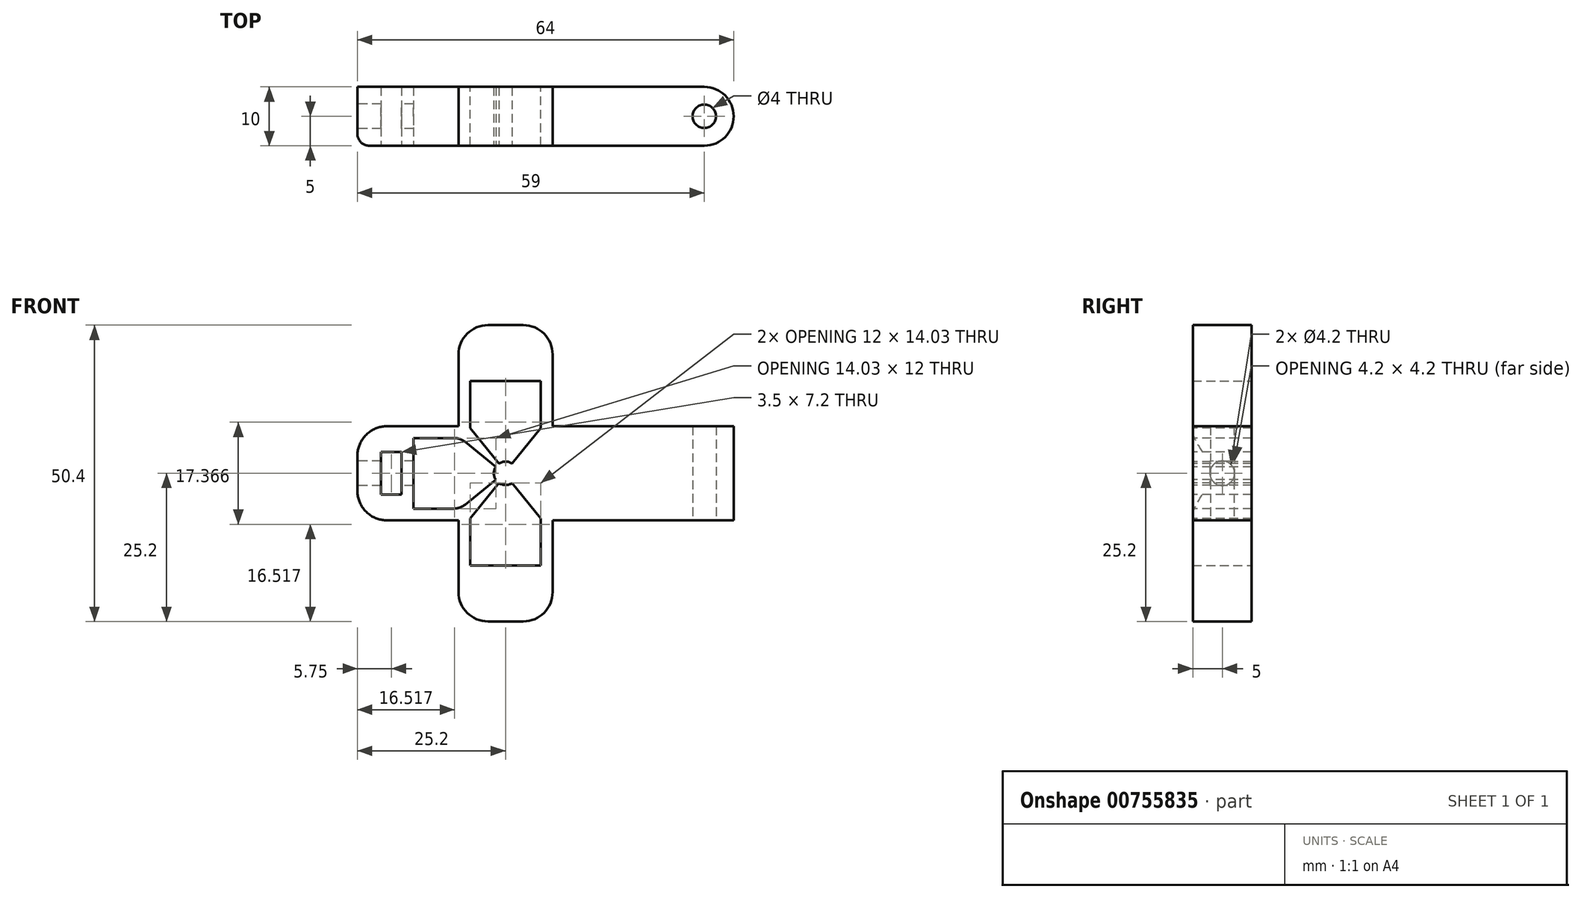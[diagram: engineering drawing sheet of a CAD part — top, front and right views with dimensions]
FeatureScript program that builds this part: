
annotation { "Feature Type Name" : "Feature", "Feature Type Description" : "" }
export const myFeature = defineFeature(function(context is Context, id is Id, definition is map)
    precondition{}
    {
        {
            var Q0;
            Q0=qCreatedBy(makeId("Top.planeOp"),FACE);
            var sketch = newSketch(context, id + "F0", { "sketchPlane" : qUnion([Q0])});
            skLineSegment(sketch, "E0.bottom", {"start": v(32, 5) * mm, "end": v(-32, 5) * mm});
            skLineSegment(sketch, "E0.top", {"start": v(32, -5) * mm, "end": v(-30, -5) * mm});
            skLineSegment(sketch, "E0.left", {"start": v(32, 5) * mm, "end": v(32, -5) * mm});
            skLineSegment(sketch, "E0.right", {"start": v(-32, 5) * mm, "end": v(-32, -3) * mm});
            skPoint(sketch, "E0.middle", {"position": v(0, 0) * mm});
            skCircle(sketch, "E1", {"center": v(27, 0) * mm, "radius": 2 * mm});
            skLineSegment(sketch, "E2", {"start": v(18, 5) * mm, "end": v(18, 19.7) * mm});
            skLineSegment(sketch, "E3", {"start": v(18, 19.7) * mm, "end": v(8, 19.7) * mm});
            skLineSegment(sketch, "E4", {"start": v(8, 19.7) * mm, "end": v(8, 5) * mm});
            skArc(sketch, "E5", {"start": v(27, -5) * mm, "mid": v(32, 0) * mm, "end": v(27, 5) * mm});
            skArc(sketch, "E6", {"start": v(-32, -3) * mm, "mid": v(-31.41, -4.41) * mm, "end": v(-30, -5) * mm});
            skLineSegment(sketch, "E7", {"start": v(-30, -3) * mm, "end": v(-30, -5) * mm});
            skLineSegment(sketch, "E8", {"start": v(-30, -3) * mm, "end": v(-32, -3) * mm});
            skSolve(sketch);
        }
        {
            var Q0;
            Q0=makeQuery(id+"F0.imprint","IMPRINT",FACE,{"disambiguationData":[TD([[makeQuery(id+"F0.imprint","IMPRINT",EDGE,{"derivedFrom":sQuery(id+"F0.wireOp",EDGE,"E0.bottom")}),1.0]])]});
            var Q1;
            Q1=makeQuery(id+"F0.imprint","IMPRINT",FACE,{"disambiguationData":[TD([[makeQuery(id+"F0.imprint","IMPRINT",EDGE,{"derivedFrom":sQuery(id+"F0.wireOp",EDGE,"E6")}),1.0]])]});
            extrude(context, id + "F1", {"entities" : qUnion([Q0, Q1]), "depth" : 16 * mm, "offsetDistance" : 25 * mm});
        }
        {
            var Q0;
            Q0=qCreatedBy(makeId("Front.planeOp"),FACE);
            var sketch = newSketch(context, id + "F2", { "sketchPlane" : qUnion([Q0])});
            skLineSegment(sketch, "E9.bottom", {"start": v(-27, 0) * mm, "end": v(32, 0) * mm});
            skLineSegment(sketch, "E9.top", {"start": v(-27, 16) * mm, "end": v(32, 16) * mm});
            skLineSegment(sketch, "E9.left", {"start": v(-32, 5) * mm, "end": v(-32, 11) * mm});
            skLineSegment(sketch, "E9.right", {"start": v(32, 0) * mm, "end": v(32, 16) * mm});
            skArc(sketch, "E10", {"start": v(-27, 16) * mm, "mid": v(-30.54, 14.54) * mm, "end": v(-32, 11) * mm});
            skArc(sketch, "E11", {"start": v(-32, 5) * mm, "mid": v(-30.54, 1.46) * mm, "end": v(-27, 0) * mm});
            skLineSegment(sketch, "E12.bottom", {"start": v(-28, 11.6) * mm, "end": v(-24.5, 11.6) * mm});
            skLineSegment(sketch, "E12.top", {"start": v(-28, 4.4) * mm, "end": v(-24.5, 4.4) * mm});
            skLineSegment(sketch, "E12.left", {"start": v(-28, 11.6) * mm, "end": v(-28, 4.4) * mm});
            skLineSegment(sketch, "E12.right", {"start": v(-24.5, 11.6) * mm, "end": v(-24.5, 4.4) * mm});
            skPoint(sketch, "E12.middle", {"position": v(-26.25, 8) * mm});
            skLineSegment(sketch, "E13.bottom", {"start": v(-22.5, 2) * mm, "end": v(-7.1, 2) * mm});
            skLineSegment(sketch, "E13.top", {"start": v(-22.5, 14) * mm, "end": v(-7.1, 14) * mm});
            skLineSegment(sketch, "E13.left", {"start": v(-22.5, 2) * mm, "end": v(-22.5, 14) * mm});
            skLineSegment(sketch, "E13.right", {"start": v(-7.1, 2) * mm, "end": v(-7.1, 14) * mm});
            skPoint(sketch, "E13.middle", {"position": v(-14.8, 8) * mm});
            skLineSegment(sketch, "E14", {"start": v(-7.1, 8) * mm, "end": v(-14.5, 14) * mm});
            skPoint(sketch, "E15.MirrorP", {"position": v(-8.7, 15.53) * mm});
            skLineSegment(sketch, "E16", {"start": v(-7.1, 8) * mm, "end": v(-14.5, 2) * mm});
            skPoint(sketch, "E16.endSnap0", {"position": v(-14.8, 2) * mm});
            skLineSegment(sketch, "E17", {"start": v(-27, 16) * mm, "end": v(-32, 16) * mm});
            skLineSegment(sketch, "E18", {"start": v(-32, 16) * mm, "end": v(-32, 11) * mm});
            skLineSegment(sketch, "E19", {"start": v(-32, 5) * mm, "end": v(-32, 0) * mm});
            skLineSegment(sketch, "E20", {"start": v(-32, 0) * mm, "end": v(-32, 5) * mm});
            skLineSegment(sketch, "E21", {"start": v(-32, 0) * mm, "end": v(-27, 0) * mm});
            skLineSegment(sketch, "E22.1.0", {"start": v(-6.8, 8.3) * mm, "end": v(-0.8, 15.7) * mm});
            skLineSegment(sketch, "E22.1.1", {"start": v(-0.8, 23.7) * mm, "end": v(-0.8, 8.3) * mm});
            skLineSegment(sketch, "E22.1.2", {"start": v(-12.8, 23.7) * mm, "end": v(-0.8, 23.7) * mm});
            skLineSegment(sketch, "E22.1.3", {"start": v(-12.8, 23.7) * mm, "end": v(-12.8, 8.3) * mm});
            skLineSegment(sketch, "E22.1.4", {"start": v(-6.8, 8.3) * mm, "end": v(-12.8, 15.7) * mm});
            skPoint(sketch, "E22.center", {"position": v(-6.8, 8) * mm});
            skLineSegment(sketch, "E22.anchor1", {"start": v(-6.8, 8) * mm, "end": v(-22.5, 2) * mm, "construction": true});
            skLineSegment(sketch, "E22.anchor2", {"start": v(-6.8, 8) * mm, "end": v(-12.8, 23.7) * mm, "construction": true});
            skLineSegment(sketch, "E23.1.0", {"start": v(-12.8, -7.7) * mm, "end": v(-12.8, 7.7) * mm});
            skLineSegment(sketch, "E23.1.1", {"start": v(-6.8, 7.7) * mm, "end": v(-12.8, 0.3) * mm});
            skLineSegment(sketch, "E23.1.2", {"start": v(-6.8, 7.7) * mm, "end": v(-0.8, 0.3) * mm});
            skLineSegment(sketch, "E23.1.3", {"start": v(-0.8, -7.7) * mm, "end": v(-0.8, 7.7) * mm});
            skLineSegment(sketch, "E23.1.4", {"start": v(-0.8, -7.7) * mm, "end": v(-12.8, -7.7) * mm});
            skLineSegment(sketch, "E24", {"start": v(1.2, 16) * mm, "end": v(1.2, 33.2) * mm});
            skLineSegment(sketch, "E25", {"start": v(1.2, 33.2) * mm, "end": v(-14.8, 33.2) * mm});
            skLineSegment(sketch, "E26", {"start": v(-14.8, 33.2) * mm, "end": v(-14.8, 16) * mm});
            skLineSegment(sketch, "E27", {"start": v(1.2, 0) * mm, "end": v(1.2, -17.2) * mm});
            skLineSegment(sketch, "E28", {"start": v(1.2, -17.2) * mm, "end": v(-14.8, -17.2) * mm});
            skLineSegment(sketch, "E29", {"start": v(-14.8, -17.2) * mm, "end": v(-14.8, 0) * mm});
            skCircle(sketch, "E30", {"center": v(-6.8, 8) * mm, "radius": 2 * mm});
            skSolve(sketch);
        }
        {
            var Q0;
            Q0=makeQuery(id+"F2.imprint","IMPRINT",FACE,{"disambiguationData":[TD([[makeQuery(id+"F2.imprint","IMPRINT",EDGE,{"derivedFrom":sQuery(id+"F2.wireOp",EDGE,"E10")}),-1.0]])]});
            var Q1;
            Q1=makeQuery(id+"F2.imprint","IMPRINT",FACE,{"disambiguationData":[TD([[makeQuery(id+"F2.imprint","IMPRINT",EDGE,{"derivedFrom":sQuery(id+"F2.wireOp",EDGE,"E11")}),-1.0]])]});
            var Q2;
            Q2=makeQuery(id+"F2.imprint","IMPRINT",FACE,{"disambiguationData":[TD([[makeQuery(id+"F2.imprint","IMPRINT",EDGE,{"derivedFrom":sQuery(id+"F2.wireOp",EDGE,"E12.bottom")}),-1.0]])]});
            var Q3;
            {var subQ0=sQuery(id+"F2.wireOp",EDGE,"E13.left");Q3=makeQuery(id+"F2.imprint","IMPRINT",FACE,{"disambiguationData":[TD([[makeQuery(id+"F2.imprint","IMPRINT",EDGE,{"derivedFrom":subQ0}),-1.0]])]});}
            extrude(context, id + "F3", {"entities" : qUnion([Q0, Q1, Q2, Q3]), "operationType" : NewBodyOperationType.REMOVE, "oppositeDirection" : true, "depth" : 5 * mm, "offsetDistance" : 25 * mm});
        }
        {
            var Q0;
            Q0=makeQuery(id+"F2.imprint","IMPRINT",FACE,{"disambiguationData":[TD([[makeQuery(id+"F2.imprint","IMPRINT",EDGE,{"derivedFrom":sQuery(id+"F2.wireOp",EDGE,"E12.bottom")}),-1.0]])]});
            var Q1;
            {var subQ0=sQuery(id+"F2.wireOp",EDGE,"E13.left");Q1=makeQuery(id+"F2.imprint","IMPRINT",FACE,{"disambiguationData":[TD([[makeQuery(id+"F2.imprint","IMPRINT",EDGE,{"derivedFrom":subQ0}),-1.0]])]});}
            var Q2;
            Q2=makeQuery(id+"F2.imprint","IMPRINT",FACE,{"disambiguationData":[TD([[makeQuery(id+"F2.imprint","IMPRINT",EDGE,{"derivedFrom":sQuery(id+"F2.wireOp",EDGE,"E10")}),-1.0]])]});
            var Q3;
            Q3=makeQuery(id+"F2.imprint","IMPRINT",FACE,{"disambiguationData":[TD([[makeQuery(id+"F2.imprint","IMPRINT",EDGE,{"derivedFrom":sQuery(id+"F2.wireOp",EDGE,"E11")}),-1.0]])]});
            extrude(context, id + "F4", {"entities" : qUnion([Q0, Q1, Q2, Q3]), "operationType" : NewBodyOperationType.REMOVE, "depth" : 5 * mm, "offsetDistance" : 25 * mm});
        }
        {
            var Q0;
            Q0=qCreatedBy(makeId("Right.planeOp"),FACE);
            cPlane(context, id + "F5", {"entities" : qUnion([Q0]), "cplaneType" : CPlaneType.OFFSET, "offset" : 32 * mm, "oppositeDirection" : true, "width" : 150 * mm, "height" : 150 * mm});
        }
        {
            var Q0;
            Q0=qCreatedBy(id+"F5.planeOp",FACE);
            var sketch = newSketch(context, id + "F6", { "sketchPlane" : qUnion([Q0])});
            skLineSegment(sketch, "E31.bottom", {"start": v(-5, 16) * mm, "end": v(5, 16) * mm});
            skLineSegment(sketch, "E31.top", {"start": v(-5, 0) * mm, "end": v(5, 0) * mm});
            skLineSegment(sketch, "E31.left", {"start": v(-5, 16) * mm, "end": v(-5, 0) * mm});
            skLineSegment(sketch, "E31.right", {"start": v(5, 16) * mm, "end": v(5, 0) * mm});
            skPoint(sketch, "E31.middle", {"position": v(0, 8) * mm});
            skCircle(sketch, "E32", {"center": v(0, 8) * mm, "radius": 2.1 * mm});
            skSolve(sketch);
        }
        {
            var Q0;
            Q0=makeQuery(id+"F6.imprint","IMPRINT",FACE,{"disambiguationData":[TD([[makeQuery(id+"F6.imprint","IMPRINT",EDGE,{"derivedFrom":sQuery(id+"F6.wireOp",EDGE,"E32")}),1.0]])]});
            extrude(context, id + "F7", {"entities" : qUnion([Q0]), "operationType" : NewBodyOperationType.REMOVE, "depth" : 10 * mm, "offsetDistance" : 25 * mm});
        }
        {
            var Q0;
            {var subQ0=sQuery(id+"F2.wireOp",EDGE,"E16");var subQ1=sQuery(id+"F2.wireOp",EDGE,"E13.bottom");Q0=makeQuery(id+"F4.boolean.opBoolean","MERGE",EDGE,{"derivedFrom":[makeQuery(id+"F3.boolean.opBoolean","COPY",EDGE,{"derivedFrom":makeQuery(id+"F3.opExtrude","SWEPT_EDGE",EDGE,{"disambiguationData":[OSD([subQ1,subQ0])]})}),makeQuery(id+"F4.opExtrude","SWEPT_EDGE",EDGE,{"disambiguationData":[OSD([subQ1,subQ0])]})]});}
            var Q1;
            {var subQ0=sQuery(id+"F2.wireOp",EDGE,"E14");var subQ1=sQuery(id+"F2.wireOp",EDGE,"E13.top");Q1=makeQuery(id+"F4.boolean.opBoolean","MERGE",EDGE,{"derivedFrom":[makeQuery(id+"F3.boolean.opBoolean","COPY",EDGE,{"derivedFrom":makeQuery(id+"F3.opExtrude","SWEPT_EDGE",EDGE,{"disambiguationData":[OSD([subQ1,subQ0])]})}),makeQuery(id+"F4.opExtrude","SWEPT_EDGE",EDGE,{"disambiguationData":[OSD([subQ1,subQ0])]})]});}
            fillet(context, id + "F8", {"entities" : qUnion([Q0, Q1]), "radius" : 3 * mm, "tangentPropagation" : true, "allowEdgeOverflow" : false});
        }
        {
            var Q0;
            {var subQ0=sQuery(id+"F2.wireOp",EDGE,"E22.1.2");Q0=makeQuery(id+"F2.imprint","IMPRINT",FACE,{"disambiguationData":[TD([[makeQuery(id+"F2.imprint","IMPRINT",EDGE,{"derivedFrom":subQ0}),1.0]])]});}
            var Q1;
            {var subQ0=sQuery(id+"F2.wireOp",EDGE,"E23.1.4");Q1=makeQuery(id+"F2.imprint","IMPRINT",FACE,{"disambiguationData":[TD([[makeQuery(id+"F2.imprint","IMPRINT",EDGE,{"derivedFrom":subQ0}),1.0]])]});}
            extrude(context, id + "F9", {"entities" : qUnion([Q0, Q1]), "operationType" : NewBodyOperationType.ADD, "depth" : 5 * mm, "offsetDistance" : 25 * mm});
        }
        {
            var Q0;
            {var subQ0=sQuery(id+"F2.wireOp",EDGE,"E22.1.2");Q0=makeQuery(id+"F2.imprint","IMPRINT",FACE,{"disambiguationData":[TD([[makeQuery(id+"F2.imprint","IMPRINT",EDGE,{"derivedFrom":subQ0}),1.0]])]});}
            var Q1;
            {var subQ0=sQuery(id+"F2.wireOp",EDGE,"E23.1.4");Q1=makeQuery(id+"F2.imprint","IMPRINT",FACE,{"disambiguationData":[TD([[makeQuery(id+"F2.imprint","IMPRINT",EDGE,{"derivedFrom":subQ0}),1.0]])]});}
            extrude(context, id + "F10", {"entities" : qUnion([Q0, Q1]), "operationType" : NewBodyOperationType.ADD, "oppositeDirection" : true, "depth" : 5 * mm, "offsetDistance" : 25 * mm});
        }
        {
            var Q0;
            {var subQ10=sQuery(id+"F2.wireOp",EDGE,"E23.1.0");var subQ12=sQuery(id+"F2.wireOp",EDGE,"E9.bottom");var subQ13=makeQuery(id+"F2.imprint","INTERSECT",VERTEX,{"derivedFrom":[subQ12,subQ10]});Q0=makeQuery(id+"F2.imprint","IMPRINT",FACE,{"disambiguationData":[TD([[makeQuery(id+"F2.imprint","IMPRINT",EDGE,{"disambiguationData":[TD([[subQ13,-1.0]])],"derivedFrom":subQ12}),1.0]])]});}
            var Q1;
            {var subQ0=sQuery(id+"F2.wireOp",EDGE,"E13.right");var subQ1=sQuery(id+"F2.wireOp",EDGE,"E13.bottom");var subQ2=makeQuery(id+"F2.imprint","INTERSECT",VERTEX,{"derivedFrom":[subQ1,subQ0]});Q1=makeQuery(id+"F2.imprint","IMPRINT",FACE,{"disambiguationData":[TD([[makeQuery(id+"F2.imprint","IMPRINT",EDGE,{"disambiguationData":[TD([[subQ2,1.0]])],"derivedFrom":subQ1}),1.0]])]});}
            var Q2;
            {var subQ6=sQuery(id+"F2.wireOp",EDGE,"E22.1.3");var subQ13=sQuery(id+"F2.wireOp",EDGE,"E9.top");var subQ14=makeQuery(id+"F2.imprint","INTERSECT",VERTEX,{"derivedFrom":[subQ13,subQ6]});Q2=makeQuery(id+"F2.imprint","IMPRINT",FACE,{"disambiguationData":[TD([[makeQuery(id+"F2.imprint","IMPRINT",EDGE,{"disambiguationData":[TD([[subQ14,-1.0]])],"derivedFrom":subQ13}),-1.0]])]});}
            var Q3;
            {var subQ0=sQuery(id+"F2.wireOp",EDGE,"E13.right");var subQ1=sQuery(id+"F2.wireOp",EDGE,"E13.top");var subQ2=makeQuery(id+"F2.imprint","INTERSECT",VERTEX,{"derivedFrom":[subQ1,subQ0]});Q3=makeQuery(id+"F2.imprint","IMPRINT",FACE,{"disambiguationData":[TD([[makeQuery(id+"F2.imprint","IMPRINT",EDGE,{"disambiguationData":[TD([[subQ2,1.0]])],"derivedFrom":subQ1}),-1.0]])]});}
            extrude(context, id + "F11", {"entities" : qUnion([Q0, Q1, Q2, Q3]), "operationType" : NewBodyOperationType.REMOVE, "oppositeDirection" : true, "depth" : 5 * mm, "offsetDistance" : 25 * mm});
        }
        {
            var Q0;
            {var subQ10=sQuery(id+"F2.wireOp",EDGE,"E23.1.0");var subQ12=sQuery(id+"F2.wireOp",EDGE,"E9.bottom");var subQ13=makeQuery(id+"F2.imprint","INTERSECT",VERTEX,{"derivedFrom":[subQ12,subQ10]});Q0=makeQuery(id+"F2.imprint","IMPRINT",FACE,{"disambiguationData":[TD([[makeQuery(id+"F2.imprint","IMPRINT",EDGE,{"disambiguationData":[TD([[subQ13,-1.0]])],"derivedFrom":subQ12}),1.0]])]});}
            var Q1;
            {var subQ0=sQuery(id+"F2.wireOp",EDGE,"E13.right");var subQ1=sQuery(id+"F2.wireOp",EDGE,"E13.bottom");var subQ2=makeQuery(id+"F2.imprint","INTERSECT",VERTEX,{"derivedFrom":[subQ1,subQ0]});Q1=makeQuery(id+"F2.imprint","IMPRINT",FACE,{"disambiguationData":[TD([[makeQuery(id+"F2.imprint","IMPRINT",EDGE,{"disambiguationData":[TD([[subQ2,1.0]])],"derivedFrom":subQ1}),1.0]])]});}
            var Q2;
            {var subQ6=sQuery(id+"F2.wireOp",EDGE,"E22.1.3");var subQ13=sQuery(id+"F2.wireOp",EDGE,"E9.top");var subQ14=makeQuery(id+"F2.imprint","INTERSECT",VERTEX,{"derivedFrom":[subQ13,subQ6]});Q2=makeQuery(id+"F2.imprint","IMPRINT",FACE,{"disambiguationData":[TD([[makeQuery(id+"F2.imprint","IMPRINT",EDGE,{"disambiguationData":[TD([[subQ14,-1.0]])],"derivedFrom":subQ13}),-1.0]])]});}
            var Q3;
            {var subQ0=sQuery(id+"F2.wireOp",EDGE,"E13.right");var subQ1=sQuery(id+"F2.wireOp",EDGE,"E13.top");var subQ2=makeQuery(id+"F2.imprint","INTERSECT",VERTEX,{"derivedFrom":[subQ1,subQ0]});Q3=makeQuery(id+"F2.imprint","IMPRINT",FACE,{"disambiguationData":[TD([[makeQuery(id+"F2.imprint","IMPRINT",EDGE,{"disambiguationData":[TD([[subQ2,1.0]])],"derivedFrom":subQ1}),-1.0]])]});}
            extrude(context, id + "F12", {"entities" : qUnion([Q0, Q1, Q2, Q3]), "operationType" : NewBodyOperationType.REMOVE, "depth" : 5 * mm, "offsetDistance" : 25 * mm});
        }
        {
            var Q0;
            {var subQ0=sQuery(id+"F2.wireOp",EDGE,"E26");var subQ1=sQuery(id+"F2.wireOp",EDGE,"E25");Q0=makeQuery(id+"F10.boolean.opBoolean","MERGE",EDGE,{"derivedFrom":[makeQuery(id+"F9.opExtrude","SWEPT_EDGE",EDGE,{"disambiguationData":[OSD([subQ1,subQ0])]}),makeQuery(id+"F10.opExtrude","SWEPT_EDGE",EDGE,{"disambiguationData":[OSD([subQ1,subQ0])]})]});}
            var Q1;
            {var subQ0=sQuery(id+"F2.wireOp",EDGE,"E25");var subQ1=sQuery(id+"F2.wireOp",EDGE,"E24");Q1=makeQuery(id+"F10.boolean.opBoolean","MERGE",EDGE,{"derivedFrom":[makeQuery(id+"F9.opExtrude","SWEPT_EDGE",EDGE,{"disambiguationData":[OSD([subQ1,subQ0])]}),makeQuery(id+"F10.opExtrude","SWEPT_EDGE",EDGE,{"disambiguationData":[OSD([subQ1,subQ0])]})]});}
            var Q2;
            {var subQ0=sQuery(id+"F2.wireOp",EDGE,"E29");var subQ1=sQuery(id+"F2.wireOp",EDGE,"E28");Q2=makeQuery(id+"F10.boolean.opBoolean","MERGE",EDGE,{"derivedFrom":[makeQuery(id+"F9.opExtrude","SWEPT_EDGE",EDGE,{"disambiguationData":[OSD([subQ1,subQ0])]}),makeQuery(id+"F10.opExtrude","SWEPT_EDGE",EDGE,{"disambiguationData":[OSD([subQ1,subQ0])]})]});}
            var Q3;
            {var subQ0=sQuery(id+"F2.wireOp",EDGE,"E28");var subQ1=sQuery(id+"F2.wireOp",EDGE,"E27");Q3=makeQuery(id+"F10.boolean.opBoolean","MERGE",EDGE,{"derivedFrom":[makeQuery(id+"F9.opExtrude","SWEPT_EDGE",EDGE,{"disambiguationData":[OSD([subQ1,subQ0])]}),makeQuery(id+"F10.opExtrude","SWEPT_EDGE",EDGE,{"disambiguationData":[OSD([subQ1,subQ0])]})]});}
            fillet(context, id + "F13", {"entities" : qUnion([Q0, Q1, Q2, Q3]), "radius" : 5 * mm, "tangentPropagation" : true, "allowEdgeOverflow" : false});
        }
    });
